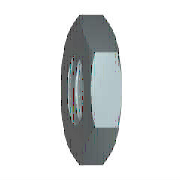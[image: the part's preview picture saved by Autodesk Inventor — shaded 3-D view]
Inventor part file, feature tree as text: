
AUTODESK INVENTOR PART (.ipt)
format: ipt  version: 2020 (Build 240168000, 168)  size: 166,400 bytes
history: native  units: mm (DEFAULTED — no unit token found)
features: sketch x3, chamfer x1, hole x1, other x1, plane x1
ambient origin geometry x7: Origin, YZ Plane, XZ Plane, X Axis, Y Axis, Z Axis, Center Point
bodies: Solid1 (feature_tree), Body (feature_tree)
feature tree (7):
  chamfer  "Chamfer1"  Angle=30.0deg  [1 undecoded]
  hole  "Thread"  [1 undecoded]
  other  "Work Axis1"
  plane  "Work Plane1"
  sketch  "Sketch1"  dims[d0=6.350853mm]
  sketch  "Sketch2"  dims[d1=1.8mm]
  sketch  "Sketch3"  dims[d2=0.0mm d3=30.0deg d4=30.0deg d5=4.6mm d6=4.6mm d7=90.0deg d25=2.459mm d26=6.0mm d27=4.0mm d28=2.0mm d29=14.3117mm d30=8.0mm d31=20.594885mm d8=0.270633mm d9=30.0deg d10=0.270633mm d11=30.0deg d13=0.0mm d14=0.0mm d39=0.0mm d40=0.270633mm d41=0.270633mm d42=0.0mm]
note: 2 required parameter values undecoded (feature->parameter linkage not recoverable at this tier; creation-order binding heuristic only, values carry confidence <= 0.55)
